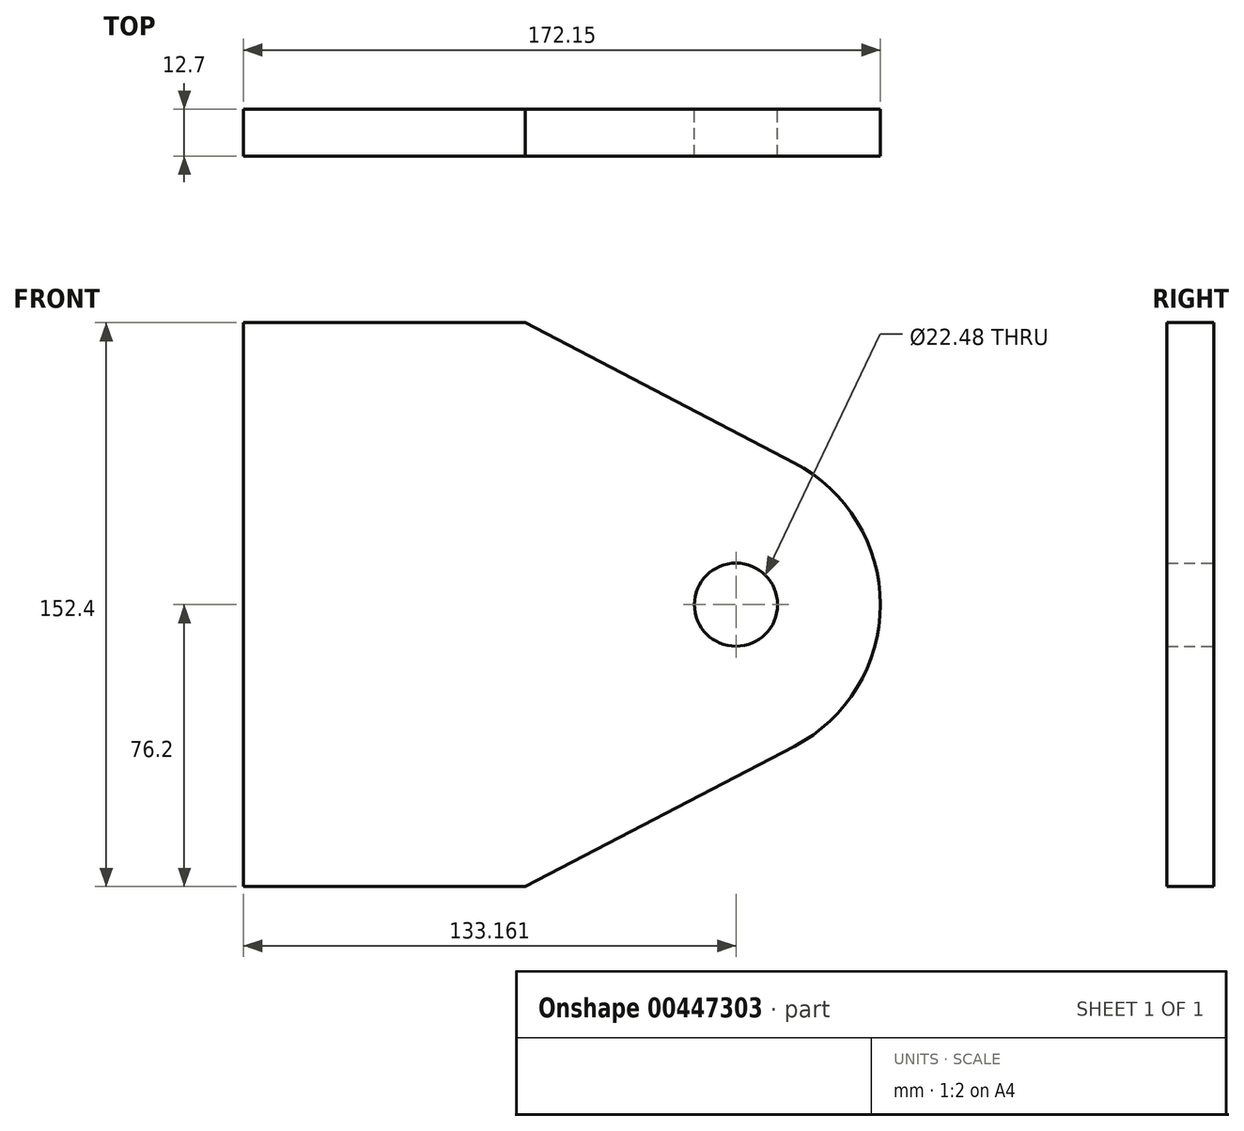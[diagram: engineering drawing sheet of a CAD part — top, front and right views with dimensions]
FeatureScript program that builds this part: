
annotation { "Feature Type Name" : "Feature", "Feature Type Description" : "" }
export const myFeature = defineFeature(function(context is Context, id is Id, definition is map)
    precondition{}
    {
        {
            var Q0;
            Q0=qCreatedBy(makeId("Front.planeOp"),FACE);
            var sketch = newSketch(context, id + "F0", { "sketchPlane" : qUnion([Q0])});
            skLineSegment(sketch, "E0", {"start": v(-112.19, 76.2) * mm, "end": v(-112.19, -76.2) * mm});
            skLineSegment(sketch, "E1", {"start": v(-112.19, 0) * mm, "end": v(154.13, 0) * mm, "construction": true});
            skLineSegment(sketch, "E2", {"start": v(-112.19, 76.2) * mm, "end": v(-35.99, 76.2) * mm});
            skLineSegment(sketch, "E3", {"start": v(-112.19, -76.2) * mm, "end": v(-35.99, -76.2) * mm});
            skLineSegment(sketch, "E4", {"start": v(-35.99, 76.2) * mm, "end": v(36.71, 38.32) * mm});
            skLineSegment(sketch, "E5.MirrorCS", {"start": v(-35.99, -76.2) * mm, "end": v(36.71, -38.32) * mm});
            skArc(sketch, "E6", {"start": v(36.71, -38.32) * mm, "mid": v(59.96, 0) * mm, "end": v(36.71, 38.32) * mm});
            skLineSegment(sketch, "E7", {"start": v(-35.99, -27.07) * mm, "end": v(-35.99, 26.84) * mm, "construction": true});
            skPoint(sketch, "E8", {"position": v(20.97, 0) * mm});
            skLineSegment(sketch, "E9", {"start": v(21.16, 20.08) * mm, "end": v(21.16, -21.63) * mm, "construction": true});
            skSolve(sketch);
        }
        {
            var Q0;
            Q0 = qSketchRegion(id + "F0", true);
            extrude(context, id + "F1", {"entities" : qUnion([Q0]), "depth" : 12.7 * mm});
        }
        {
            var Q0;
            Q0=sQuery(id+"F0.wireOp",VERTEX,"E8");
            var Q1;
            Q1=makeQuery(id+"F1.opExtrude","SWEPT_BODY",BODY,{"disambiguationData":[OSD([sQuery(id+"F0.wireOp",EDGE,"E0"),sQuery(id+"F0.wireOp",EDGE,"E2"),sQuery(id+"F0.wireOp",EDGE,"E3"),sQuery(id+"F0.wireOp",EDGE,"E4"),sQuery(id+"F0.wireOp",EDGE,"E5.MirrorCS"),sQuery(id+"F0.wireOp",EDGE,"E6")])]});
            hole(context, id + "F2", {"style" : HoleStyle.SIMPLE, "endStyle" : HoleEndStyle.THROUGH, "oppositeDirection" : true, "holeDiameter" : 22.48 * mm, "isTappedThrough" : true, "tappedDepth" : 12.7 * mm, "tapClearance" : 3, "locations" : qUnion([Q0]), "scope" : qUnion([Q1])});
        }
    });
